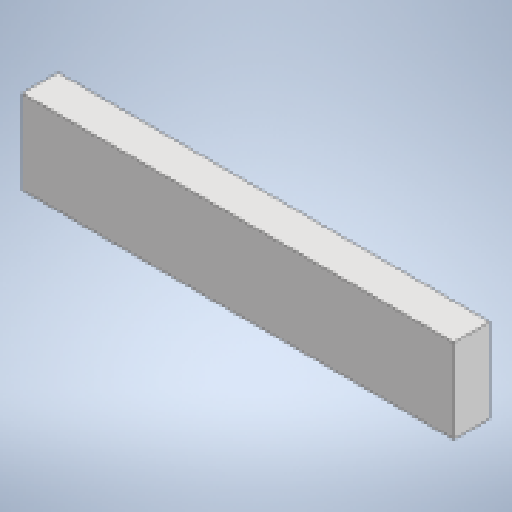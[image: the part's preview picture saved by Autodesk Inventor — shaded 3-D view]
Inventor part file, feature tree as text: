
AUTODESK INVENTOR PART (.ipt)
format: ipt  version: 2025.1 (Build 291241020, 241B)  size: 120,832 bytes
history: native  units: in
note: dims shown in document units (in); Inventor stores cm internally (conversion verified against a paired STEP export)
features: other x4, reference x2, extrude x1, sketch x1
ambient origin geometry x8: Origin, YZ Plane, XZ Plane, XY Plane, X Axis, Y Axis, Z Axis, Center Point
bodies: Solid1 (feature_tree)
feature tree (8):
  extrude  "Extrusion1"  Depth=1.5in TaperAngle=0.0deg
  sketch  "Sketch1"  dims[d0=3.5in d1=1.5in d2=0.0in]
  reference  "Reference1"
  reference  "Reference2"
  other  "<userpath>\Documents\Tburn24\F_Legs2\F_Legs2.iam"
  other  "F_Legs2.iam"
  other  "side-side:2"
  other  "side-side:1"
